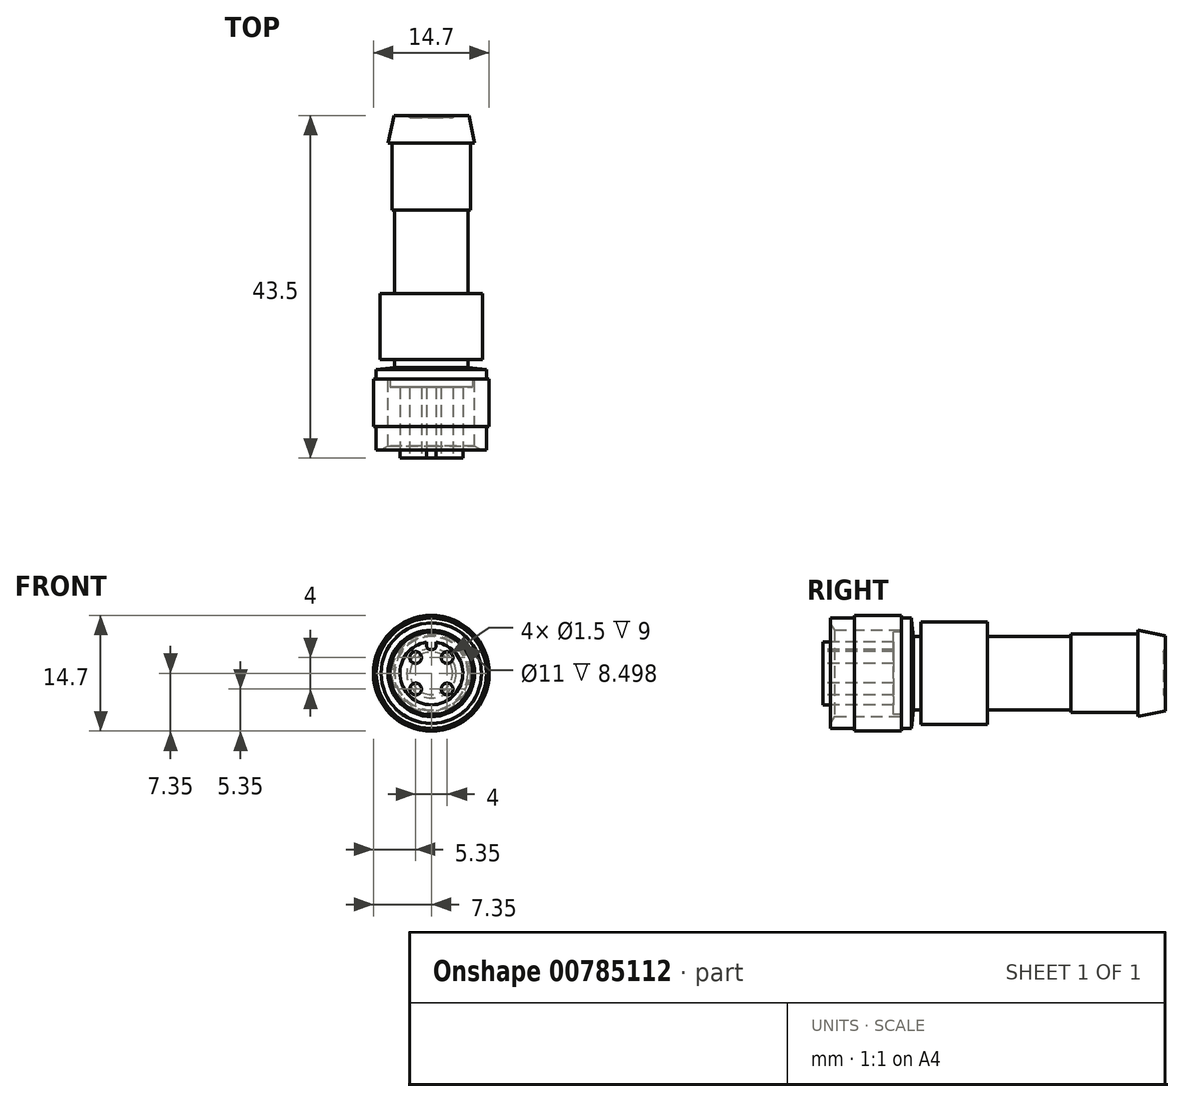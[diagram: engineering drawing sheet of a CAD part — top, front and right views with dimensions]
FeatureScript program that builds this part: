
annotation { "Feature Type Name" : "Feature", "Feature Type Description" : "" }
export const myFeature = defineFeature(function(context is Context, id is Id, definition is map)
    precondition{}
    {
        {
            var Q0;
            Q0=qCreatedBy(makeId("Right.planeOp"),FACE);
            var sketch = newSketch(context, id + "F0", { "sketchPlane" : qUnion([Q0])});
            skLineSegment(sketch, "E0", {"start": v(0, 7) * mm, "end": v(1.25, 7) * mm});
            skLineSegment(sketch, "E1", {"start": v(1.25, 7) * mm, "end": v(1.5, 4.65) * mm});
            skLineSegment(sketch, "E2", {"start": v(1.5, 4.65) * mm, "end": v(2.5, 4.65) * mm});
            skLineSegment(sketch, "E3", {"start": v(2.5, 4.65) * mm, "end": v(2.5, 6.5) * mm});
            skLineSegment(sketch, "E4", {"start": v(2.5, 6.5) * mm, "end": v(10.9, 6.5) * mm});
            skLineSegment(sketch, "E5", {"start": v(10.9, 6.5) * mm, "end": v(10.9, 4.65) * mm});
            skLineSegment(sketch, "E6", {"start": v(10.9, 4.65) * mm, "end": v(21.5, 4.65) * mm});
            skLineSegment(sketch, "E7", {"start": v(21.5, 5) * mm, "end": v(21.5, 4.65) * mm});
            skLineSegment(sketch, "E8", {"start": v(21.5, 5) * mm, "end": v(30, 5) * mm});
            skLineSegment(sketch, "E9", {"start": v(30, 5) * mm, "end": v(30, 5.5) * mm});
            skLineSegment(sketch, "E10", {"start": v(30, 5.5) * mm, "end": v(33.5, 4.76) * mm});
            skLineSegment(sketch, "E11", {"start": v(33.5, 4.76) * mm, "end": v(33.5, 3.13) * mm});
            skLineSegment(sketch, "E12", {"start": v(33.5, 3.13) * mm, "end": v(33.25, 2.7) * mm});
            skLineSegment(sketch, "E13", {"start": v(33.25, 2.7) * mm, "end": v(33.25, 0) * mm});
            skLineSegment(sketch, "E14", {"start": v(33.25, 0) * mm, "end": v(0, 0) * mm});
            skLineSegment(sketch, "E15", {"start": v(0, 0) * mm, "end": v(0, 7) * mm});
            skLineSegment(sketch, "E16", {"start": v(0, 0) * mm, "end": v(-34.2, 0) * mm, "construction": true});
            skSolve(sketch);
        }
        {
            var Q0;
            Q0 = qSketchRegion(id + "F0", true);
            var Q1;
            Q1=sQuery(id+"F0.wireOp",EDGE,"E16");
            revolve(context, id + "F1", {"surfaceOperationType" : NewSurfaceOperationType.NEW, "entities" : qUnion([Q0]), "axis" : qUnion([Q1]), "revolveType" : RevolveType.FULL});
        }
        {
            var Q0;
            Q0=qCreatedBy(makeId("Right.planeOp"),FACE);
            var sketch = newSketch(context, id + "F2", { "sketchPlane" : qUnion([Q0])});
            skLineSegment(sketch, "E17", {"start": v(0, 5.5) * mm, "end": v(0, 7.35) * mm});
            skLineSegment(sketch, "E18", {"start": v(-6, 7.35) * mm, "end": v(-6, 7) * mm});
            skLineSegment(sketch, "E19", {"start": v(-6, 7) * mm, "end": v(-9, 7) * mm});
            skLineSegment(sketch, "E20", {"start": v(-9, 7) * mm, "end": v(-9, 6.37) * mm});
            skLineSegment(sketch, "E21", {"start": v(-9, 6.37) * mm, "end": v(-8.5, 5.5) * mm});
            skLineSegment(sketch, "E22", {"start": v(-8.5, 5.5) * mm, "end": v(0, 5.5) * mm});
            skLineSegment(sketch, "E23", {"start": v(-6, 7.35) * mm, "end": v(0, 7.35) * mm});
            skLineSegment(sketch, "E24", {"start": v(0, 0) * mm, "end": v(-25.5, 0) * mm, "construction": true});
            skSolve(sketch);
        }
        {
            var Q0;
            Q0 = qSketchRegion(id + "F2", true);
            var Q1;
            Q1=sQuery(id+"F2.wireOp",EDGE,"E24");
            revolve(context, id + "F3", {"operationType" : NewBodyOperationType.ADD, "surfaceOperationType" : NewSurfaceOperationType.NEW, "entities" : qUnion([Q0]), "axis" : qUnion([Q1]), "revolveType" : RevolveType.FULL});
        }
        {
            var Q0;
            Q0=qCreatedBy(makeId("Right.planeOp"),FACE);
            var sketch = newSketch(context, id + "F4", { "sketchPlane" : qUnion([Q0])});
            skLineSegment(sketch, "E25", {"start": v(0, 0) * mm, "end": v(0, 5.25) * mm});
            skLineSegment(sketch, "E26", {"start": v(0, 5.25) * mm, "end": v(-1, 5.25) * mm});
            skLineSegment(sketch, "E27", {"start": v(-1, 5.25) * mm, "end": v(-1, 4) * mm});
            skLineSegment(sketch, "E28", {"start": v(-1, 4) * mm, "end": v(-10, 4) * mm});
            skLineSegment(sketch, "E29", {"start": v(-10, 4) * mm, "end": v(-10, 0) * mm});
            skLineSegment(sketch, "E30", {"start": v(-10, 0) * mm, "end": v(0, 0) * mm});
            skSolve(sketch);
        }
        {
            var Q0;
            Q0 = qSketchRegion(id + "F4", true);
            var Q1;
            Q1=sQuery(id+"F4.wireOp",EDGE,"E30");
            revolve(context, id + "F5", {"operationType" : NewBodyOperationType.ADD, "surfaceOperationType" : NewSurfaceOperationType.NEW, "entities" : qUnion([Q0]), "axis" : qUnion([Q1]), "revolveType" : RevolveType.FULL});
        }
        {
            var Q0;
            Q0=makeQuery(id+"F5.opRevolve","SWEPT_FACE",FACE,{"disambiguationData":[OSD([sQuery(id+"F4.wireOp",EDGE,"E29")])]});
            var sketch = newSketch(context, id + "F6", { "sketchPlane" : qUnion([Q0])});
            skLineSegment(sketch, "E31.bottom", {"start": v(-2, 2) * mm, "end": v(2, 2) * mm, "construction": true});
            skLineSegment(sketch, "E31.top", {"start": v(-2, -2) * mm, "end": v(2, -2) * mm, "construction": true});
            skLineSegment(sketch, "E31.left", {"start": v(-2, 2) * mm, "end": v(-2, -2) * mm, "construction": true});
            skLineSegment(sketch, "E31.right", {"start": v(2, 2) * mm, "end": v(2, -2) * mm, "construction": true});
            skPoint(sketch, "E31.middle", {"position": v(0, 0) * mm});
            skCircle(sketch, "E32", {"center": v(-2, 2) * mm, "radius": 0.75 * mm});
            skCircle(sketch, "E33", {"center": v(2, 2) * mm, "radius": 0.75 * mm});
            skCircle(sketch, "E34", {"center": v(2, -2) * mm, "radius": 0.75 * mm});
            skCircle(sketch, "E35", {"center": v(-2, -2) * mm, "radius": 0.75 * mm});
            skLineSegment(sketch, "E36.bottom", {"start": v(-0.1, 3) * mm, "end": v(0.1, 3) * mm});
            skLineSegment(sketch, "E36.top", {"start": v(-0.6, 4.5) * mm, "end": v(0.6, 4.5) * mm});
            skLineSegment(sketch, "E36.left", {"start": v(-0.6, 3.5) * mm, "end": v(-0.6, 4.5) * mm});
            skLineSegment(sketch, "E36.right", {"start": v(0.6, 3.5) * mm, "end": v(0.6, 4.5) * mm});
            skPoint(sketch, "E37", {"position": v(0, 3) * mm});
            skPoint(sketch, "E38.visualSharp", {"position": v(-0.6, 3) * mm});
            skArc(sketch, "E38.filletArc", {"start": v(-0.6, 3.5) * mm, "mid": v(-0.45, 3.15) * mm, "end": v(-0.1, 3) * mm});
            skPoint(sketch, "E39.visualSharp", {"position": v(0.6, 3) * mm});
            skArc(sketch, "E39.filletArc", {"start": v(0.1, 3) * mm, "mid": v(0.45, 3.15) * mm, "end": v(0.6, 3.5) * mm});
            skSolve(sketch);
        }
        {
            var Q0;
            Q0 = qSketchRegion(id + "F6", true);
            var Q1;
            Q1=makeQuery(id+"F5.opRevolve","SWEPT_FACE",FACE,{"disambiguationData":[OSD([sQuery(id+"F4.wireOp",EDGE,"E27")])]});
            extrude(context, id + "F7", {"entities" : qUnion([Q0]), "operationType" : NewBodyOperationType.REMOVE, "endBound" : BoundingType.UP_TO_SURFACE, "oppositeDirection" : true, "depth" : 25 * mm, "endBoundEntityFace" : qUnion([Q1]), "offsetDistance" : 25 * mm});
        }
    });
